# Revit family: STORA-LK_D1200
name_source: partatom
category: Leuchten
revit_build: Autodesk Revit 2017 (Build: 20160225_1515(x64)
units: mm (PartAtom-declared; Revit-internal decimal feet)

## family parameters
Basisbauteil = Fläche
Beim Laden mit Abzugskörper schneiden = Nein
Bemaßung runder Anschluss = Durchmesser verwenden
Gemeinsam genutzt = Nein
Lichtquelle = Ja
Raumberechnungspunkt = Nein
Teiletyp = Normal

## types (8) — shared parameters
Beschreibung = Suspended lumnaire
Body = RIDI Metal White 9016
Certification = CE
Cover = RIDI Light Emitting Surface
Diameter = 1200 mm
Emissionsform beim Rendern sichtbar = Nein
Energy Class = A++ - A
Farbfilter = 16777215
Farbtemperaturverschiebung bei Dämpfen der Lampe = <Keine Auswahl>
Height = 100 mm  [stored 0.328084 ft]
Hersteller = Spectral
IP Rating = IP 20
Lampe = 1xLED-M
Neigungswinkel = -90.00°
Suspension = RIDI Metall silver 9006
Voltage = 230 V
Von Kreisdurchmesser aussenden = 1184 mm  [stored 3.88451 ft]
Weight = 16.5 kg
zero-valued in all types: Vorgabe-Ansicht

## per-type parameters (varying)
| type | Datei für fotometrisches Netz | Indirect | Modell | Number of Poles | Scheinlast |
| STORA-LK-LED D1200/830 OS | STORA-LK-LED D1200_840 OS.IES | RIDI Metal White 9016 | SPC0620052 | 1 | 70 VA |
| STORA-LK-LED D1200/840 OS | STORA-LK-LED D1200_840 OS.IES | RIDI Metal White 9016 | SPC0620053 | 1 | 70 VA |
| STORA-LK-I-LED D1200/830 OS | STORA-LK-I-LED D1200_840 OS.IES | RIDI Light Emitting Surface | SPC0620054 | 2 | 127 VA |
| STORA-LK-I-LED D1200/840 OS | STORA-LK-I-LED D1200_840 OS.IES | RIDI Light Emitting Surface | SPC0620055 | 2 | 127 VA |
| STORA-LK-I-LED D1200/840 OS-DA | STORA-LK-I-LED D1200_840 OS.IES | RIDI Light Emitting Surface | SPC0630055 | 1 | 127 VA |
| STORA-LK-I-LED D1200/830 OS-DA | STORA-LK-I-LED D1200_840 OS.IES | RIDI Light Emitting Surface | SPC0630054 | 1 | 127 VA |
| STORA-LK-LED D1200/830 OS-DA | STORA-LK-LED D1200_840 OS.IES | RIDI Metal White 9016 | SPC0630052 | 1 | 70 VA |
| STORA-LK-LED D1200/840 OS-DA | STORA-LK-LED D1200_840 OS.IES | RIDI Metal White 9016 | SPC0630053 | 1 | 70 VA |

note: [stored X ft] marks values corroborated as IEEE doubles in the binary element streams (Revit-internal decimal feet)

## geometry (parser evidence)
native form markers: Sweep x3
no freeform markers — native parametric forms only
